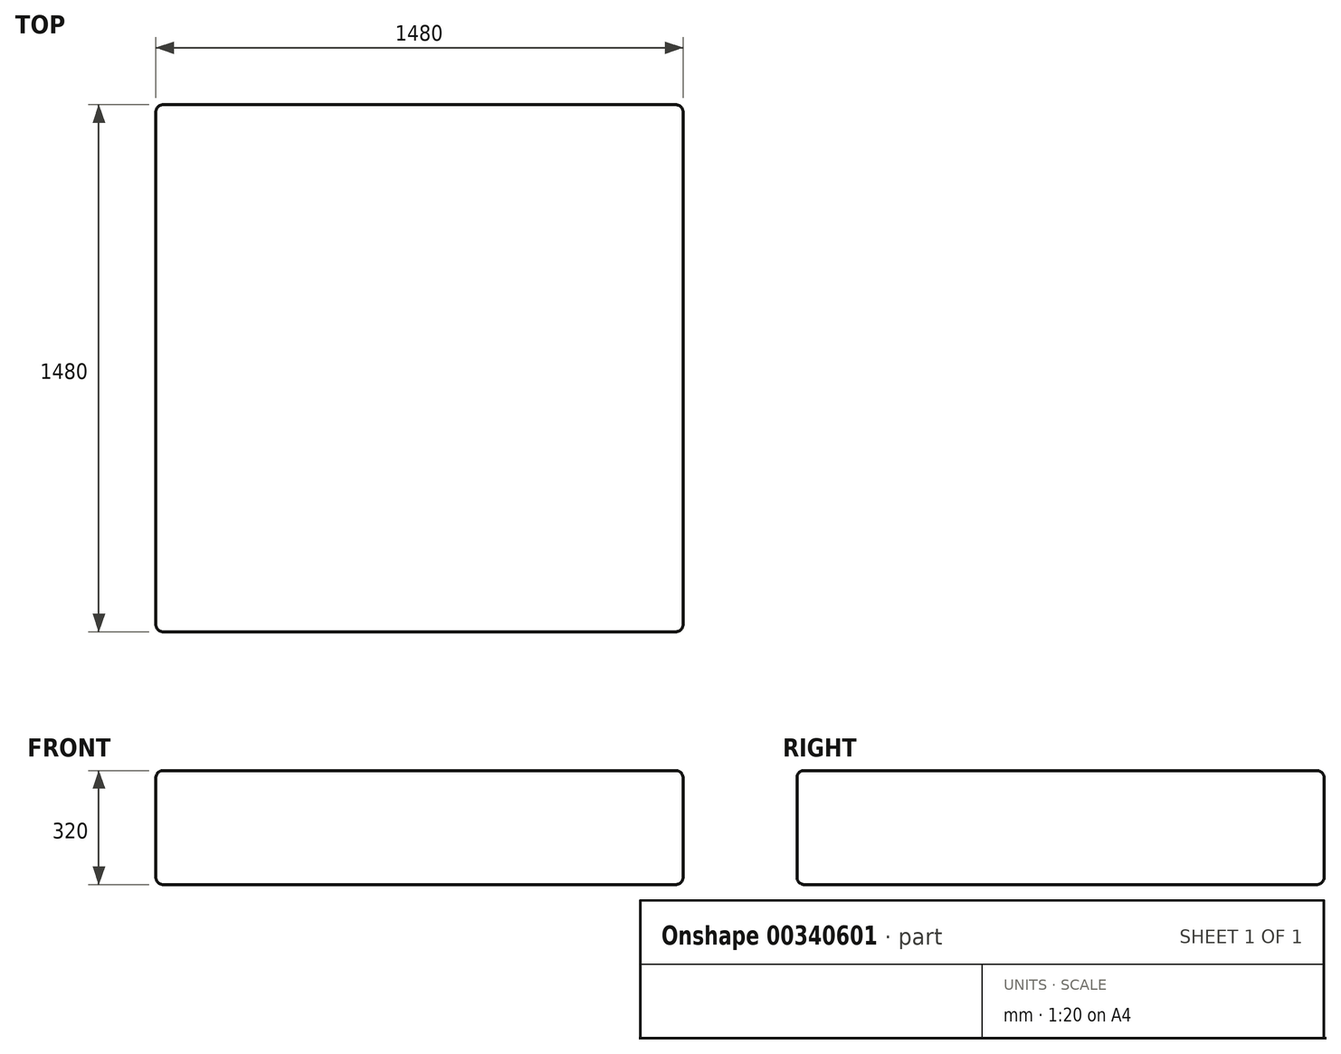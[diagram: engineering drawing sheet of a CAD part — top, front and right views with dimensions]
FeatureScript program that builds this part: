
annotation { "Feature Type Name" : "Feature", "Feature Type Description" : "" }
export const myFeature = defineFeature(function(context is Context, id is Id, definition is map)
    precondition{}
    {
        {
            var Q0;
            Q0=qCreatedBy(makeId("Top.planeOp"),FACE);
            var sketch = newSketch(context, id + "F0", { "sketchPlane" : qUnion([Q0])});
            skLineSegment(sketch, "E0.bottom", {"start": v(-60.6, 1434.4) * mm, "end": v(1419.4, 1434.4) * mm});
            skLineSegment(sketch, "E0.top", {"start": v(-60.6, -45.6) * mm, "end": v(1419.4, -45.6) * mm});
            skLineSegment(sketch, "E0.left", {"start": v(-60.6, 1434.4) * mm, "end": v(-60.6, -45.6) * mm});
            skLineSegment(sketch, "E0.right", {"start": v(1419.4, 1434.4) * mm, "end": v(1419.4, -45.6) * mm});
            skSolve(sketch);
        }
        {
            var Q0;
            Q0=makeQuery(id+"F0.imprint","IMPRINT",FACE,{"disambiguationData":[TD([[makeQuery(id+"F0.imprint","IMPRINT",EDGE,{"derivedFrom":sQuery(id+"F0.wireOp",EDGE,"E0.bottom")}),-1.0]])]});
            extrude(context, id + "F1", {"entities" : qUnion([Q0]), "depth" : 320 * mm});
        }
        {
            var Q0;
            Q0=makeQuery(id+"F1.opExtrude","CAP_EDGE",EDGE,{"disambiguationData":[OSD([sQuery(id+"F0.wireOp",EDGE,"E0.left")])],"isStart":false});
            var Q1;
            Q1=makeQuery(id+"F1.opExtrude","CAP_FACE",FACE,{"disambiguationData":[OSD([sQuery(id+"F0.wireOp",EDGE,"E0.bottom"),sQuery(id+"F0.wireOp",EDGE,"E0.top"),sQuery(id+"F0.wireOp",EDGE,"E0.left"),sQuery(id+"F0.wireOp",EDGE,"E0.right")])],"isStart":false});
            var Q2;
            Q2=makeQuery(id+"F1.opExtrude","SWEPT_FACE",FACE,{"disambiguationData":[OSD([sQuery(id+"F0.wireOp",EDGE,"E0.top")])]});
            var Q3;
            Q3=makeQuery(id+"F1.opExtrude","SWEPT_FACE",FACE,{"disambiguationData":[OSD([sQuery(id+"F0.wireOp",EDGE,"E0.left")])]});
            var Q4;
            Q4=makeQuery(id+"F1.opExtrude","CAP_FACE",FACE,{"disambiguationData":[OSD([sQuery(id+"F0.wireOp",EDGE,"E0.bottom"),sQuery(id+"F0.wireOp",EDGE,"E0.top"),sQuery(id+"F0.wireOp",EDGE,"E0.left"),sQuery(id+"F0.wireOp",EDGE,"E0.right")])],"isStart":true});
            var Q5;
            Q5=makeQuery(id+"F1.opExtrude","SWEPT_FACE",FACE,{"disambiguationData":[OSD([sQuery(id+"F0.wireOp",EDGE,"E0.right")])]});
            var Q6;
            Q6=makeQuery(id+"F1.opExtrude","SWEPT_FACE",FACE,{"disambiguationData":[OSD([sQuery(id+"F0.wireOp",EDGE,"E0.bottom")])]});
            fillet(context, id + "F2", {"entities" : qUnion([Q0, Q1, Q2, Q3, Q4, Q5, Q6]), "radius" : 20 * mm, "tangentPropagation" : true, "allowEdgeOverflow" : false});
        }
    });
